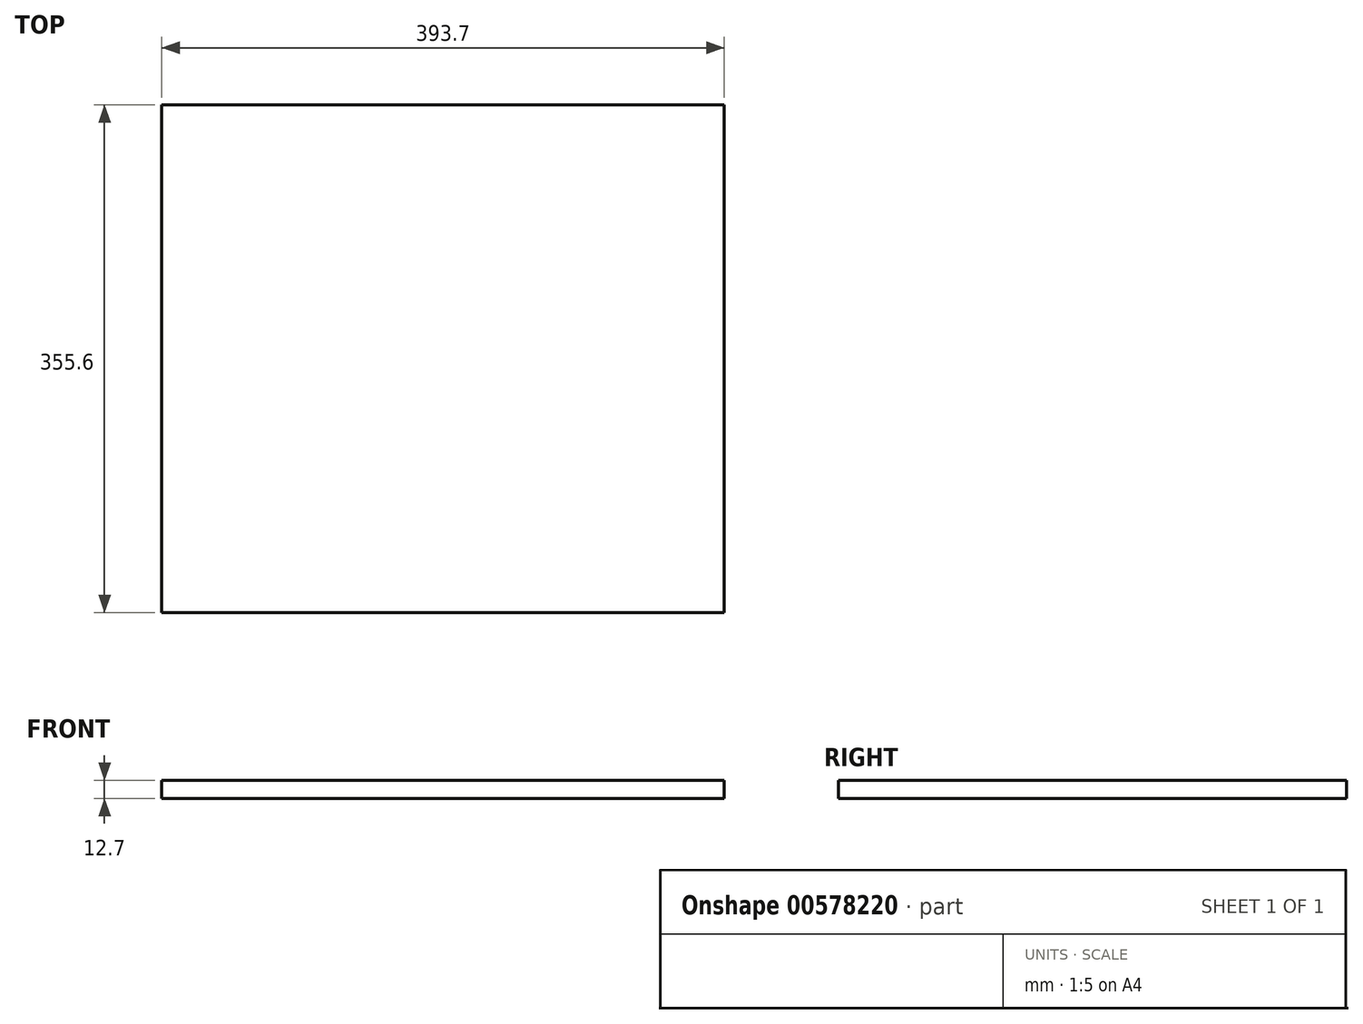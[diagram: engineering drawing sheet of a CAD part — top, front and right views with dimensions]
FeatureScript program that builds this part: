
annotation { "Feature Type Name" : "Feature", "Feature Type Description" : "" }
export const myFeature = defineFeature(function(context is Context, id is Id, definition is map)
    precondition{}
    {
        {
            var Q0;
            Q0=qCreatedBy(makeId("Top.planeOp"),FACE);
            var sketch = newSketch(context, id + "F0", { "sketchPlane" : qUnion([Q0])});
            skLineSegment(sketch, "E0.bottom", {"start": v(-237.68, 143.58) * mm, "end": v(156.02, 143.58) * mm});
            skLineSegment(sketch, "E0.top", {"start": v(-237.68, -212.02) * mm, "end": v(156.02, -212.02) * mm});
            skLineSegment(sketch, "E0.left", {"start": v(-237.68, 143.58) * mm, "end": v(-237.68, -212.02) * mm});
            skLineSegment(sketch, "E0.right", {"start": v(156.02, 143.58) * mm, "end": v(156.02, -212.02) * mm});
            skSolve(sketch);
        }
        {
            var Q0;
            Q0=makeQuery(id+"F0.imprint","IMPRINT",FACE,{"disambiguationData":[TD([[makeQuery(id+"F0.imprint","IMPRINT",EDGE,{"derivedFrom":sQuery(id+"F0.wireOp",EDGE,"E0.bottom")}),-1.0]])]});
            extrude(context, id + "F1", {"entities" : qUnion([Q0]), "depth" : 12.7 * mm, "offsetDistance" : 25.4 * mm});
        }
    });
